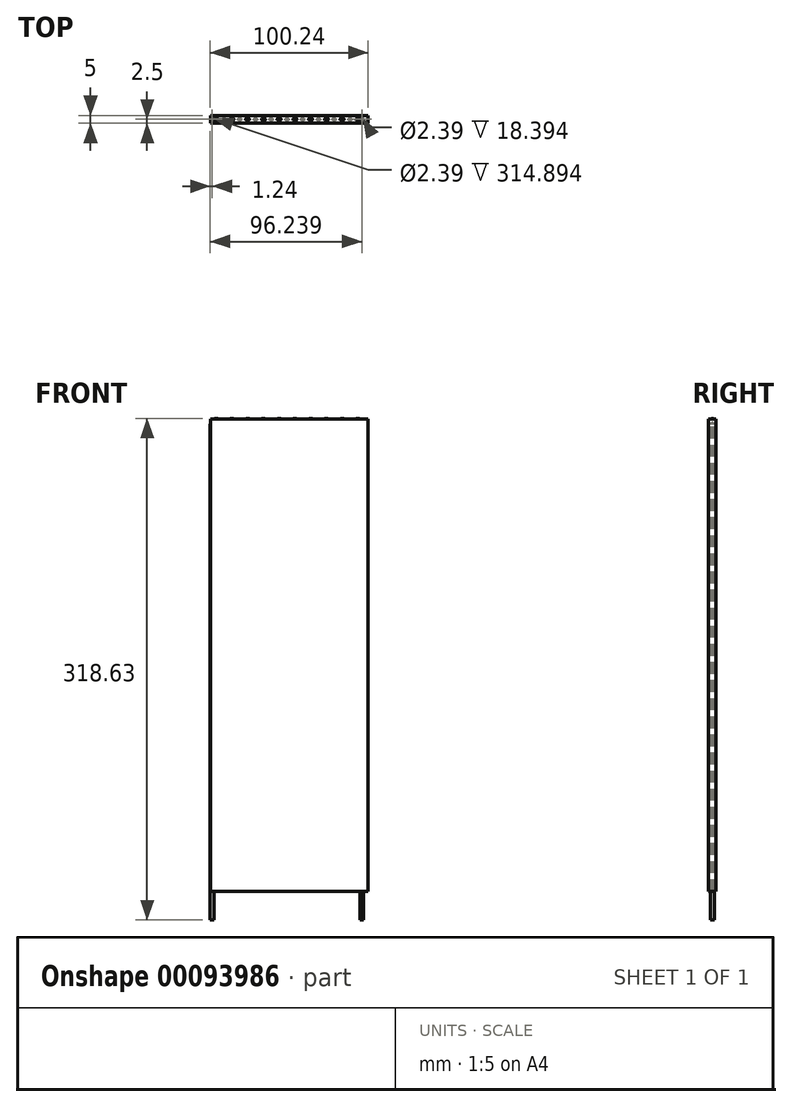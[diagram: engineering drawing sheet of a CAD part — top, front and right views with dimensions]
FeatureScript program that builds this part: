
annotation { "Feature Type Name" : "Feature", "Feature Type Description" : "" }
export const myFeature = defineFeature(function(context is Context, id is Id, definition is map)
    precondition{}
    {
        {
            var Q0;
            Q0=qCreatedBy(makeId("Front.planeOp"),FACE);
            var sketch = newSketch(context, id + "F0", { "sketchPlane" : qUnion([Q0])});
            skLineSegment(sketch, "E0.bottom", {"start": v(-51.4, 228.97) * mm, "end": v(48.6, 228.97) * mm});
            skLineSegment(sketch, "E0.top", {"start": v(-51.4, -71.03) * mm, "end": v(48.6, -71.03) * mm});
            skLineSegment(sketch, "E0.left", {"start": v(-51.4, 228.97) * mm, "end": v(-51.4, -71.03) * mm});
            skLineSegment(sketch, "E0.right", {"start": v(48.6, 228.97) * mm, "end": v(48.6, -71.03) * mm});
            skArc(sketch, "E1", {"start": v(-45.4, 225.47) * mm, "mid": v(-47.9, 227.97) * mm, "end": v(-50.4, 225.47) * mm});
            skArc(sketch, "E2", {"start": v(-35.4, 225.47) * mm, "mid": v(-37.9, 227.97) * mm, "end": v(-40.4, 225.47) * mm});
            skArc(sketch, "E3", {"start": v(-25.4, 225.47) * mm, "mid": v(-27.9, 227.97) * mm, "end": v(-30.4, 225.47) * mm});
            skArc(sketch, "E4", {"start": v(-15.4, 225.47) * mm, "mid": v(-17.9, 227.97) * mm, "end": v(-20.4, 225.47) * mm});
            skArc(sketch, "E5", {"start": v(-5.4, 225.47) * mm, "mid": v(-7.9, 227.97) * mm, "end": v(-10.4, 225.47) * mm});
            skArc(sketch, "E6", {"start": v(4.6, 225.47) * mm, "mid": v(2.1, 227.97) * mm, "end": v(-0.4, 225.47) * mm});
            skArc(sketch, "E7", {"start": v(14.6, 225.47) * mm, "mid": v(12.1, 227.97) * mm, "end": v(9.6, 225.47) * mm});
            skArc(sketch, "E8", {"start": v(24.6, 225.47) * mm, "mid": v(22.1, 227.97) * mm, "end": v(19.6, 225.47) * mm});
            skArc(sketch, "E9", {"start": v(34.6, 225.47) * mm, "mid": v(32.1, 227.97) * mm, "end": v(29.6, 225.47) * mm});
            skArc(sketch, "E10", {"start": v(44.6, 225.47) * mm, "mid": v(42.1, 227.97) * mm, "end": v(39.6, 225.47) * mm});
            skArc(sketch, "E11", {"start": v(-45.4, -67.53) * mm, "mid": v(-42.9, -70.03) * mm, "end": v(-40.4, -67.53) * mm});
            skArc(sketch, "E12", {"start": v(-35.4, -67.53) * mm, "mid": v(-32.9, -70.03) * mm, "end": v(-30.4, -67.53) * mm});
            skArc(sketch, "E13", {"start": v(-25.4, -67.53) * mm, "mid": v(-22.9, -70.03) * mm, "end": v(-20.4, -67.53) * mm});
            skArc(sketch, "E14", {"start": v(-15.4, -67.53) * mm, "mid": v(-12.9, -70.03) * mm, "end": v(-10.4, -67.53) * mm});
            skArc(sketch, "E15", {"start": v(-5.4, -67.53) * mm, "mid": v(-2.9, -70.03) * mm, "end": v(-0.4, -67.53) * mm});
            skArc(sketch, "E16", {"start": v(4.6, -67.53) * mm, "mid": v(7.1, -70.03) * mm, "end": v(9.6, -67.53) * mm});
            skArc(sketch, "E17", {"start": v(14.6, -67.53) * mm, "mid": v(17.1, -70.03) * mm, "end": v(19.6, -67.53) * mm});
            skArc(sketch, "E18", {"start": v(24.6, -67.53) * mm, "mid": v(27.1, -70.03) * mm, "end": v(29.6, -67.53) * mm});
            skArc(sketch, "E19", {"start": v(34.6, -67.53) * mm, "mid": v(37.1, -70.03) * mm, "end": v(39.6, -67.53) * mm});
            skLineSegment(sketch, "E20", {"start": v(-45.4, 225.47) * mm, "end": v(-45.4, -67.53) * mm});
            skLineSegment(sketch, "E21", {"start": v(-40.4, -67.53) * mm, "end": v(-40.4, 225.47) * mm});
            skLineSegment(sketch, "E22", {"start": v(-35.4, 225.47) * mm, "end": v(-35.4, -67.53) * mm});
            skLineSegment(sketch, "E23", {"start": v(-30.4, -67.53) * mm, "end": v(-30.4, 225.47) * mm});
            skLineSegment(sketch, "E24", {"start": v(-25.4, 225.47) * mm, "end": v(-25.4, -67.53) * mm});
            skLineSegment(sketch, "E25", {"start": v(-20.4, -67.53) * mm, "end": v(-20.4, 225.47) * mm});
            skLineSegment(sketch, "E26", {"start": v(-15.4, 225.47) * mm, "end": v(-15.4, -67.53) * mm});
            skLineSegment(sketch, "E27", {"start": v(-10.4, -67.53) * mm, "end": v(-10.4, 225.47) * mm});
            skLineSegment(sketch, "E28", {"start": v(-5.4, 225.47) * mm, "end": v(-5.4, -67.53) * mm});
            skPoint(sketch, "E29.endSnap0", {"position": v(-0.4, 225.47) * mm});
            skLineSegment(sketch, "E30", {"start": v(-0.4, 225.47) * mm, "end": v(-0.4, -67.53) * mm});
            skLineSegment(sketch, "E31", {"start": v(4.6, -67.53) * mm, "end": v(4.6, 225.47) * mm});
            skLineSegment(sketch, "E32", {"start": v(9.6, 225.47) * mm, "end": v(9.6, -67.53) * mm});
            skLineSegment(sketch, "E33", {"start": v(14.6, -67.53) * mm, "end": v(14.6, 225.47) * mm});
            skLineSegment(sketch, "E34", {"start": v(19.6, 225.47) * mm, "end": v(19.6, -67.53) * mm});
            skLineSegment(sketch, "E35", {"start": v(24.6, -67.53) * mm, "end": v(24.6, 225.47) * mm});
            skLineSegment(sketch, "E36", {"start": v(29.6, 225.47) * mm, "end": v(29.6, -67.53) * mm});
            skLineSegment(sketch, "E37", {"start": v(34.6, -67.53) * mm, "end": v(34.6, 225.47) * mm});
            skLineSegment(sketch, "E38", {"start": v(39.6, 225.47) * mm, "end": v(39.6, -67.53) * mm});
            skLineSegment(sketch, "E39", {"start": v(44.6, 225.47) * mm, "end": v(44.6, 69.84) * mm});
            skLineSegment(sketch, "E40", {"start": v(44.6, 69.84) * mm, "end": v(44.6, -67.53) * mm});
            skLineSegment(sketch, "E41", {"start": v(-50.4, 225.47) * mm, "end": v(-50.4, -89.42) * mm});
            skPoint(sketch, "E42.orphan", {"position": v(-42.9, 225.47) * mm});
            skPoint(sketch, "E43.orphan", {"position": v(-32.9, 225.47) * mm});
            skPoint(sketch, "E44.orphan", {"position": v(-22.9, 225.47) * mm});
            skPoint(sketch, "E45.orphan", {"position": v(-12.9, 225.47) * mm});
            skPoint(sketch, "E46.orphan", {"position": v(-2.9, 225.47) * mm});
            skPoint(sketch, "E47.orphan", {"position": v(7.1, 225.47) * mm});
            skPoint(sketch, "E48.orphan", {"position": v(17.1, 225.47) * mm});
            skPoint(sketch, "E49.orphan", {"position": v(27.1, 225.47) * mm});
            skPoint(sketch, "E50.orphan", {"position": v(37.1, 225.47) * mm});
            skLineSegment(sketch, "E51", {"start": v(44.6, -67.53) * mm, "end": v(44.6, -89.42) * mm});
            skPoint(sketch, "E52.orphan", {"position": v(-37.9, -67.53) * mm});
            skPoint(sketch, "E53.orphan", {"position": v(-27.9, -67.53) * mm});
            skPoint(sketch, "E54.orphan", {"position": v(-17.9, -67.53) * mm});
            skPoint(sketch, "E55.orphan", {"position": v(-7.9, -67.53) * mm});
            skPoint(sketch, "E56.orphan", {"position": v(2.1, -67.53) * mm});
            skPoint(sketch, "E57.orphan", {"position": v(12.1, -67.53) * mm});
            skPoint(sketch, "E58.orphan", {"position": v(22.1, -67.53) * mm});
            skPoint(sketch, "E59.orphan", {"position": v(32.1, -67.53) * mm});
            skPoint(sketch, "E60.end.orphan", {"position": v(42.1, -67.53) * mm});
            skLineSegment(sketch, "E61.bottom", {"start": v(-52.16, 229.73) * mm, "end": v(49.36, 229.73) * mm});
            skLineSegment(sketch, "E61.top", {"start": v(-52.16, -71.8) * mm, "end": v(49.36, -71.8) * mm});
            skLineSegment(sketch, "E61.left", {"start": v(-52.16, 229.73) * mm, "end": v(-52.16, -71.8) * mm});
            skLineSegment(sketch, "E61.right", {"start": v(49.36, 229.73) * mm, "end": v(49.36, -71.8) * mm});
            skSolve(sketch);
        }
        {
            var Q0;
            Q0=qCreatedBy(makeId("Top.planeOp"),FACE);
            var Q1;
            Q1=sQuery(id+"F0.wireOp",VERTEX,"E41.end");
            cPlane(context, id + "F1", {"entities" : qUnion([Q0, Q1]), "cplaneType" : CPlaneType.PLANE_POINT, "offset" : 152.4 * mm, "width" : 152.4 * mm, "height" : 152.4 * mm});
        }
        {
            var Q0;
            Q0=qCreatedBy(id+"F1.planeOp",FACE);
            var sketch = newSketch(context, id + "F2", { "sketchPlane" : qUnion([Q0])});
            skCircle(sketch, "E62", {"center": v(-50.4, 0) * mm, "radius": 1.24 * mm});
            skCircle(sketch, "E63", {"center": v(-50.4, 0) * mm, "radius": 1.2 * mm});
            skSolve(sketch);
        }
        {
            var Q0;
            Q0=makeQuery(id+"F2.imprint","IMPRINT",FACE,{"disambiguationData":[TD([[makeQuery(id+"F2.imprint","IMPRINT",EDGE,{"derivedFrom":sQuery(id+"F2.wireOp",EDGE,"E62")}),1.0]])]});
            var Q1;
            Q1=sQuery(id+"F0.wireOp",EDGE,"E41");
            var Q2;
            Q2=sQuery(id+"F0.wireOp",EDGE,"E1");
            var Q3;
            Q3=sQuery(id+"F0.wireOp",EDGE,"E20");
            var Q4;
            Q4=sQuery(id+"F0.wireOp",EDGE,"E11");
            var Q5;
            Q5=sQuery(id+"F0.wireOp",EDGE,"E21");
            var Q6;
            Q6=sQuery(id+"F0.wireOp",EDGE,"E2");
            var Q7;
            Q7=sQuery(id+"F0.wireOp",EDGE,"E22");
            var Q8;
            Q8=sQuery(id+"F0.wireOp",EDGE,"E12");
            var Q9;
            Q9=sQuery(id+"F0.wireOp",EDGE,"E23");
            var Q10;
            Q10=sQuery(id+"F0.wireOp",EDGE,"E3");
            var Q11;
            Q11=sQuery(id+"F0.wireOp",EDGE,"E24");
            var Q12;
            Q12=sQuery(id+"F0.wireOp",EDGE,"E13");
            var Q13;
            Q13=sQuery(id+"F0.wireOp",EDGE,"E25");
            var Q14;
            Q14=sQuery(id+"F0.wireOp",EDGE,"E4");
            var Q15;
            Q15=sQuery(id+"F0.wireOp",EDGE,"E26");
            var Q16;
            Q16=sQuery(id+"F0.wireOp",EDGE,"E14");
            var Q17;
            Q17=sQuery(id+"F0.wireOp",EDGE,"E27");
            var Q18;
            Q18=sQuery(id+"F0.wireOp",EDGE,"E5");
            var Q19;
            Q19=sQuery(id+"F0.wireOp",EDGE,"E28");
            var Q20;
            Q20=sQuery(id+"F0.wireOp",EDGE,"E15");
            var Q21;
            Q21=sQuery(id+"F0.wireOp",EDGE,"E30");
            var Q22;
            Q22=sQuery(id+"F0.wireOp",EDGE,"E6");
            var Q23;
            Q23=sQuery(id+"F0.wireOp",EDGE,"E31");
            var Q24;
            Q24=sQuery(id+"F0.wireOp",EDGE,"E16");
            var Q25;
            Q25=sQuery(id+"F0.wireOp",EDGE,"E32");
            var Q26;
            Q26=sQuery(id+"F0.wireOp",EDGE,"E7");
            var Q27;
            Q27=sQuery(id+"F0.wireOp",EDGE,"E33");
            var Q28;
            Q28=sQuery(id+"F0.wireOp",EDGE,"E17");
            var Q29;
            Q29=sQuery(id+"F0.wireOp",EDGE,"E34");
            var Q30;
            Q30=sQuery(id+"F0.wireOp",EDGE,"E8");
            var Q31;
            Q31=sQuery(id+"F0.wireOp",EDGE,"E35");
            var Q32;
            Q32=sQuery(id+"F0.wireOp",EDGE,"E18");
            var Q33;
            Q33=sQuery(id+"F0.wireOp",EDGE,"E36");
            var Q34;
            Q34=sQuery(id+"F0.wireOp",EDGE,"E9");
            var Q35;
            Q35=sQuery(id+"F0.wireOp",EDGE,"E37");
            var Q36;
            Q36=sQuery(id+"F0.wireOp",EDGE,"E19");
            var Q37;
            Q37=sQuery(id+"F0.wireOp",EDGE,"E38");
            var Q38;
            Q38=sQuery(id+"F0.wireOp",EDGE,"E10");
            var Q39;
            Q39=sQuery(id+"F0.wireOp",EDGE,"E51");
            var Q40;
            Q40=sQuery(id+"F0.wireOp",EDGE,"E40");
            var Q41;
            Q41=sQuery(id+"F0.wireOp",EDGE,"E39");
            sweep(context, id + "F3", {"profiles" : qUnion([Q0]), "path" : qUnion([Q1, Q2, Q3, Q4, Q5, Q6, Q7, Q8, Q9, Q10, Q11, Q12, Q13, Q14, Q15, Q16, Q17, Q18, Q19, Q20, Q21, Q22, Q23, Q24, Q25, Q26, Q27, Q28, Q29, Q30, Q31, Q32, Q33, Q34, Q35, Q36, Q37, Q38, Q39, Q40, Q41])});
        }
        {
            var Q0;
            {var subQ0=sQuery(id+"F0.wireOp",EDGE,"E1");Q0=makeQuery(id+"F0.imprint","IMPRINT",FACE,{"disambiguationData":[TD([[makeQuery(id+"F0.imprint","IMPRINT",EDGE,{"derivedFrom":subQ0}),1.0]])]});}
            var Q1;
            Q1=makeQuery(id+"F0.imprint","IMPRINT",FACE,{"disambiguationData":[TD([[makeQuery(id+"F0.imprint","IMPRINT",EDGE,{"derivedFrom":sQuery(id+"F0.wireOp",EDGE,"E0.bottom")}),-1.0]])]});
            extrude(context, id + "F4", {"entities" : qUnion([Q0, Q1]), "operationType" : NewBodyOperationType.ADD, "endBound" : BoundingType.SYMMETRIC, "depth" : 5 * mm});
        }
    });
